# Revit family: P1455_3_Hole_U_Shape_Fitting
name_source: partatom
category: Generic Models
units: mm (PartAtom-declared; Revit-internal decimal feet)

## family parameters
Always vertical = No
Can host rebar = No
Cut with Voids When Loaded = No
Part Type = Normal
Room Calculation Point = No
Round Connector Dimension = Use Diameter
Shared = No
Work Plane-Based = Yes

## types (3) — shared parameters
Cost = $0.00
Description = P1455 - 3 Hole, "U" Shape Fitting
Manufacturer = Atkore Unistrut
Model = P1455
Salsify ID1 = US-P1455
URL = https://www.atkore.com
Weight = 0.58 lb
zero-valued in all types: Default Elevation

## per-type parameters (varying)
| type | Material | UPC |
| P1455 EG | Electro Galvanized | "786364055503" |
| P1455 GR | Green | "786364020952" |
| P1455 ZD | Zinc Dichromate | "786364049625" |

note: column(s) folded — value = type name in every type: Part Number

## geometry (parser evidence)
native form markers: Sweep x2
no freeform markers — native parametric forms only
